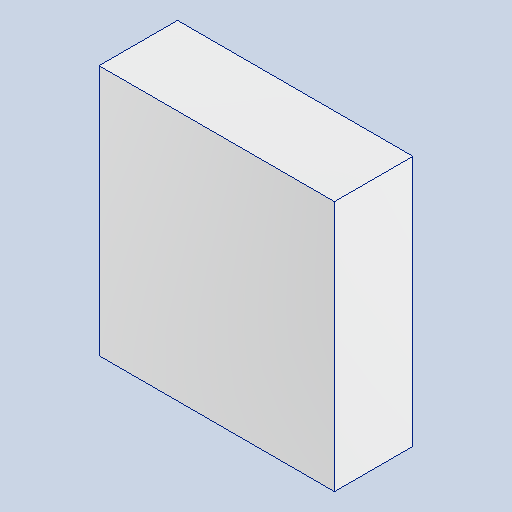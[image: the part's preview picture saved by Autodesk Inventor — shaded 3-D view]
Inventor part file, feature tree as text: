
AUTODESK INVENTOR PART (.ipt)
format: ipt  version: 2025 (Build 290162010, 162A)  size: 115,712 bytes
history: native  units: mm
features: extrude x1, sketch x1
ambient origin geometry x8: Origin, YZ Plane, XZ Plane, XY Plane, X Axis, Y Axis, Z Axis, Center Point
bodies: Volumenkörper1 (feature_tree)
feature tree (2):
  extrude  "Extrusion1"  Depth=32.0mm
  sketch  "Skizze1"  dims[d0=30.0mm d1=32.0mm d2=10.0mm d3=0.0mm]
